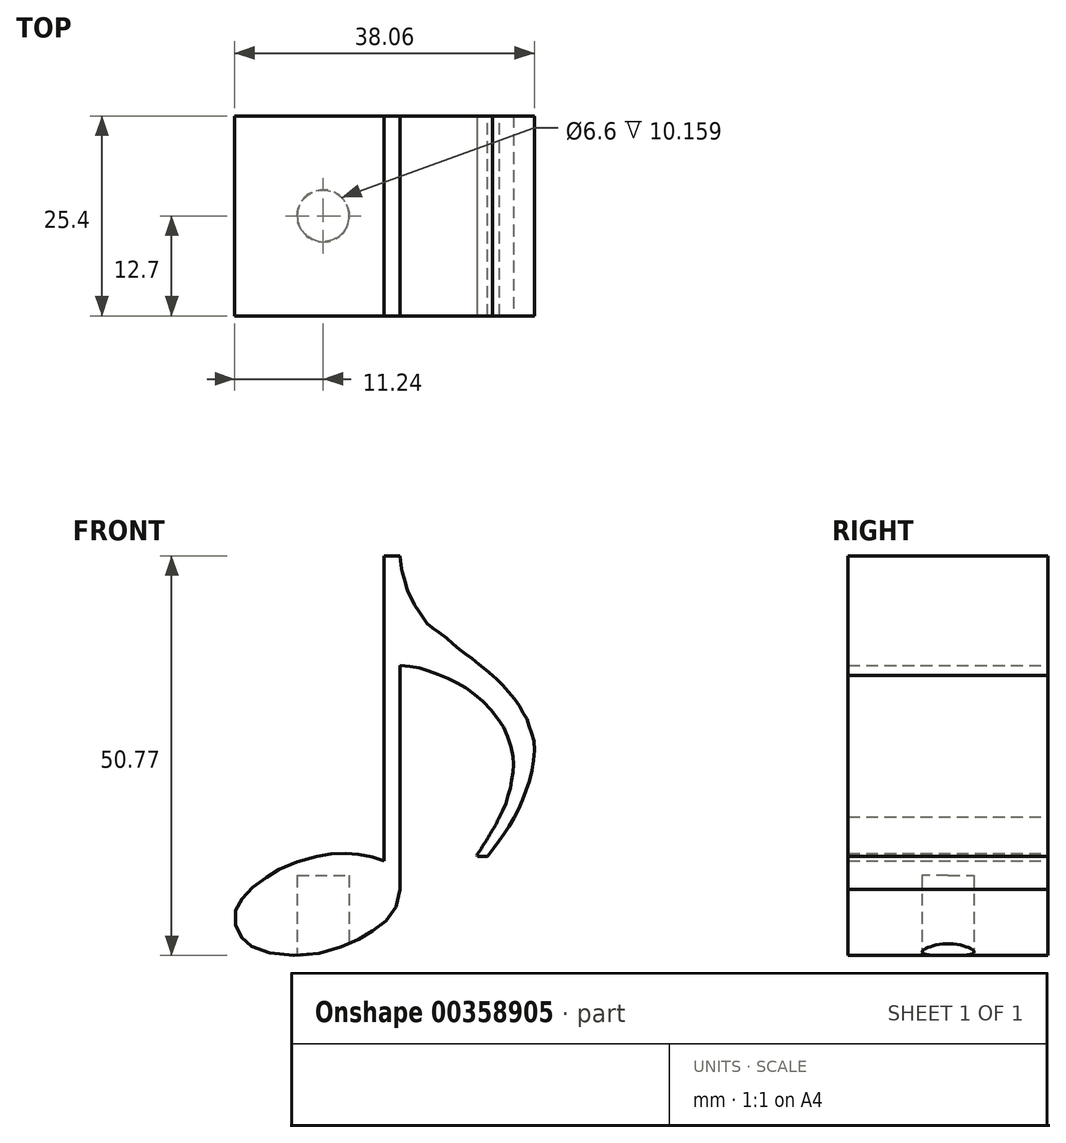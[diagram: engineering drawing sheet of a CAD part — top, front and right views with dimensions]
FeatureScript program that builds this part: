
annotation { "Feature Type Name" : "Feature", "Feature Type Description" : "" }
export const myFeature = defineFeature(function(context is Context, id is Id, definition is map)
    precondition{}
    {
        {
            var Q0;
            Q0=qCreatedBy(makeId("Top.planeOp"),FACE);
            var sketch = newSketch(context, id + "F0", { "sketchPlane" : qUnion([Q0])});
            skCircle(sketch, "E0", {"center": v(0, 0) * mm, "radius": 3.3 * mm});
            skSolve(sketch);
        }
        {
            var Q0;
            Q0=qCreatedBy(makeId("Front.planeOp"),FACE);
            var sketch = newSketch(context, id + "F1", { "sketchPlane" : qUnion([Q0])});
            skLineSegment(sketch, "E1", {"start": v(9.76, 36.88) * mm, "end": v(9.76, 8.42) * mm});
            skLineSegment(sketch, "E2", {"start": v(7.73, 12) * mm, "end": v(7.73, 50.77) * mm});
            skLineSegment(sketch, "E3", {"start": v(7.73, 50.77) * mm, "end": v(9.77, 50.77) * mm});
            skFitSpline(sketch, "E4", {"points": [v(9.77, 50.77) * mm, v(9.8, 50.17) * mm, v(9.84, 49.8) * mm, v(9.88, 49.35) * mm, v(9.97, 48.9) * mm, v(10.1, 48.41) * mm, v(10.33, 47.66) * mm, v(10.49, 47.1) * mm, v(10.68, 46.5) * mm, v(10.9, 46) * mm, v(11.54, 44.66) * mm, v(12.4, 43.37) * mm, v(13.16, 42.27) * mm, v(14.2, 41.41) * mm, v(15.78, 40.22) * mm, v(17.26, 38.93) * mm, v(18.4, 38.07) * mm, v(20.03, 36.83) * mm, v(21.5, 35.58) * mm], "startDerivative": vector(2.39, -12.18) * mm, "endDerivative": vector(19.93, -14.36) * mm});
            skFitSpline(sketch, "E5", {"points": [v(21.5, 35.58) * mm, v(22.02, 35.1) * mm, v(22.9, 34.24) * mm, v(23.93, 33.04) * mm, v(24.9, 31.8) * mm, v(25.45, 30.76) * mm, v(25.95, 29.85) * mm, v(26.24, 28.89) * mm, v(26.63, 27.81) * mm, v(26.82, 26.17) * mm, v(26.63, 24.18) * mm, v(26.14, 22.05) * mm, v(25.47, 20.16) * mm, v(24.7, 18.32) * mm, v(23.77, 16.68) * mm, v(22.9, 15.32) * mm, v(22.01, 14.08) * mm, v(20.88, 12.62) * mm], "startDerivative": vector(12.34, -10.96) * mm, "endDerivative": vector(-19.51, -22.17) * mm});
            skLineSegment(sketch, "E6", {"start": v(20.88, 12.62) * mm, "end": v(19.57, 12.62) * mm});
            skFitSpline(sketch, "E7", {"points": [v(19.57, 12.62) * mm, v(19.57, 12.83) * mm, v(20.01, 13.53) * mm, v(20.24, 13.9) * mm, v(20.65, 14.5) * mm, v(21, 15.08) * mm, v(21.36, 15.72) * mm, v(21.74, 16.33) * mm, v(22.08, 17.02) * mm, v(22.41, 17.6) * mm], "startDerivative": vector(-0.52, 2.94) * mm, "endDerivative": vector(3.99, 5.56) * mm});
            skFitSpline(sketch, "E8", {"points": [v(22.41, 17.6) * mm, v(22.65, 18.06) * mm, v(22.95, 18.79) * mm, v(23.3, 19.63) * mm, v(23.53, 20.5) * mm, v(23.76, 21.3) * mm, v(23.9, 22.05) * mm, v(24.05, 22.92) * mm, v(24.12, 23.7) * mm, v(24.17, 24.54) * mm, v(24.1, 25.35) * mm, v(23.78, 26.68) * mm, v(23.31, 28.12) * mm, v(22.69, 29.37) * mm, v(21.9, 30.43) * mm, v(20.85, 31.76) * mm, v(19.6, 32.85) * mm, v(18.47, 33.79) * mm, v(17.18, 34.53) * mm, v(15.97, 35.15) * mm, v(14.64, 35.7) * mm, v(13.4, 36.13) * mm, v(12.22, 36.52) * mm, v(11.05, 36.72) * mm, v(9.76, 36.88) * mm], "startDerivative": vector(8.17, 15.54) * mm, "endDerivative": vector(-29.21, 3.75) * mm});
            skFitSpline(sketch, "E9", {"points": [v(7.73, 12) * mm, v(6.27, 12.53) * mm, v(4.6, 12.84) * mm, v(2.98, 13) * mm, v(1.05, 12.9) * mm, v(-0.89, 12.58) * mm, v(-4.85, 11.33) * mm, v(-6.84, 10.23) * mm, v(-8.98, 8.61) * mm, v(-10.5, 7) * mm, v(-11.17, 5.48) * mm, v(-11.07, 3.55) * mm, v(-10.13, 2.03) * mm, v(-8.56, 0.94) * mm, v(-3.86, 0) * mm, v(1.67, 0.88) * mm, v(4.8, 2.24) * mm, v(7, 3.6) * mm, v(8.93, 5.53) * mm, v(9.76, 8.42) * mm], "startDerivative": vector(-34.29, 13.76) * mm, "endDerivative": vector(9.06, 53.54) * mm});
            skSolve(sketch);
        }
        {
            var Q0;
            Q0=makeQuery(id+"F1.imprint","IMPRINT",FACE,{"disambiguationData":[TD([[makeQuery(id+"F1.imprint","IMPRINT",EDGE,{"derivedFrom":sQuery(id+"F1.wireOp",EDGE,"E1")}),-1.0]])]});
            extrude(context, id + "F2", {"entities" : qUnion([Q0]), "depth" : 12.7 * mm, "hasSecondDirection" : true, "secondDirectionOppositeDirection" : true, "secondDirectionDepth" : 12.7 * mm});
        }
        {
            var Q0;
            Q0 = qSketchRegion(id + "F0", true);
            extrude(context, id + "F3", {"entities" : qUnion([Q0]), "operationType" : NewBodyOperationType.REMOVE, "depth" : 10.16 * mm});
        }
    });
